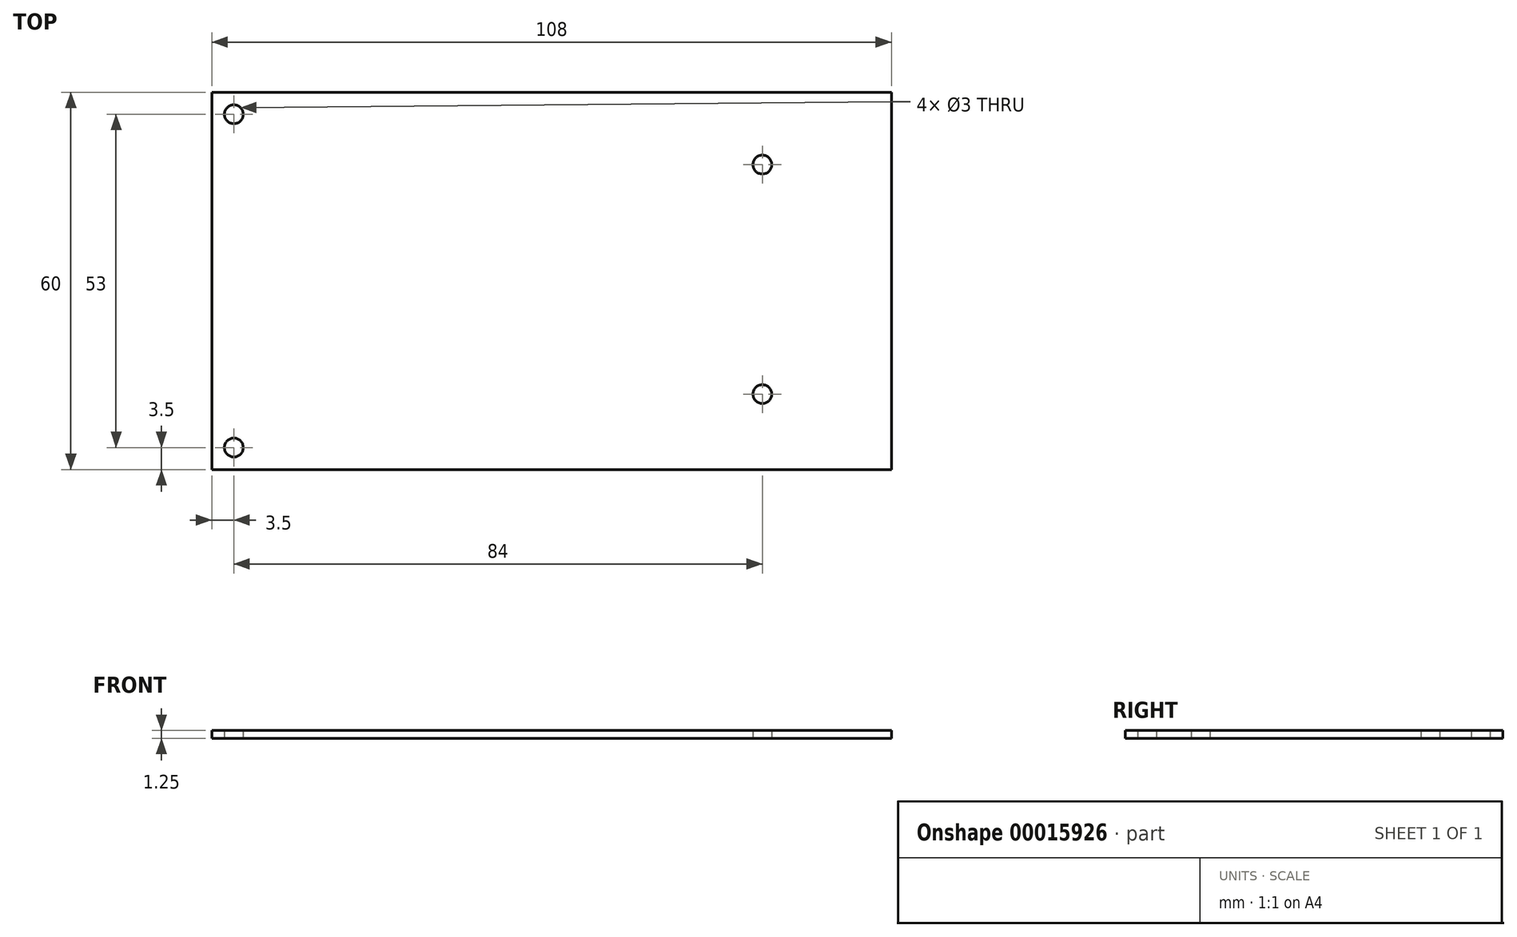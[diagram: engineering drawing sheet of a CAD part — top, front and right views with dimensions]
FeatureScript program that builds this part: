
annotation { "Feature Type Name" : "Feature", "Feature Type Description" : "" }
export const myFeature = defineFeature(function(context is Context, id is Id, definition is map)
    precondition{}
    {
        {
            var Q0;
            Q0=qCreatedBy(makeId("Top.planeOp"),FACE);
            var sketch = newSketch(context, id + "F0", { "sketchPlane" : qUnion([Q0])});
            skLineSegment(sketch, "E0.rect.bottom", {"start": v(54, -30) * mm, "end": v(-54, -30) * mm});
            skLineSegment(sketch, "E0.rect.top", {"start": v(54, 30) * mm, "end": v(-54, 30) * mm});
            skLineSegment(sketch, "E0.rect.left", {"start": v(54, -30) * mm, "end": v(54, 30) * mm});
            skLineSegment(sketch, "E0.rect.right", {"start": v(-54, -30) * mm, "end": v(-54, 30) * mm});
            skPoint(sketch, "E0.rect.middle", {"position": v(0, 0) * mm});
            skCircle(sketch, "E1", {"center": v(-50.5, 26.5) * mm, "radius": 1.5 * mm});
            skCircle(sketch, "E2", {"center": v(-50.5, -26.5) * mm, "radius": 1.5 * mm});
            skCircle(sketch, "E3", {"center": v(33.5, 18.5) * mm, "radius": 1.5 * mm});
            skCircle(sketch, "E4", {"center": v(33.5, -18) * mm, "radius": 1.5 * mm});
            skSolve(sketch);
        }
        {
            var Q0;
            Q0 = qSketchRegion(id + "F0", true);
            extrude(context, id + "F1", {"entities" : qUnion([Q0]), "depth" : 1.25 * mm});
        }
    });
